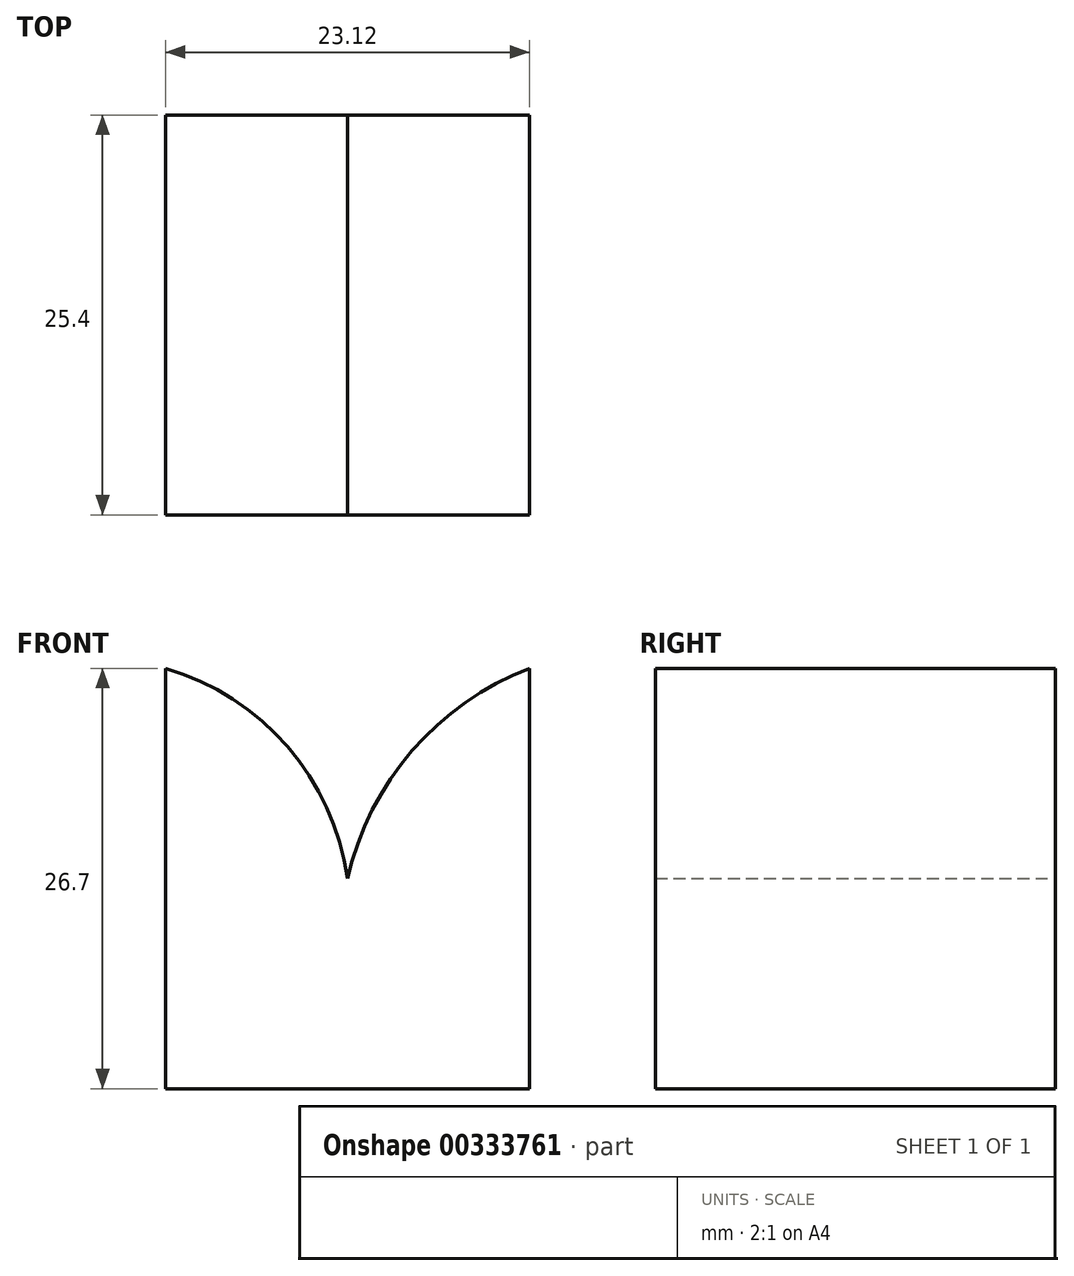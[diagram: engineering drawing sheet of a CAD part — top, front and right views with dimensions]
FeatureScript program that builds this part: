
annotation { "Feature Type Name" : "Feature", "Feature Type Description" : "" }
export const myFeature = defineFeature(function(context is Context, id is Id, definition is map)
    precondition{}
    {
        {
            var Q0;
            Q0=qCreatedBy(makeId("Front.planeOp"),FACE);
            var sketch = newSketch(context, id + "F0", { "sketchPlane" : qUnion([Q0])});
            skLineSegment(sketch, "E0.top", {"start": v(11.56, -13.35) * mm, "end": v(-11.56, -13.35) * mm});
            skLineSegment(sketch, "E0.left", {"start": v(11.56, 13.35) * mm, "end": v(11.56, -13.35) * mm});
            skLineSegment(sketch, "E0.right", {"start": v(-11.56, 13.35) * mm, "end": v(-11.56, -13.35) * mm});
            skPoint(sketch, "E0.middle", {"position": v(0, 0) * mm});
            skArc(sketch, "E1", {"start": v(11.56, 13.35) * mm, "mid": v(4.11, 8.12) * mm, "end": v(0, 0) * mm});
            skArc(sketch, "E2", {"start": v(0, 0) * mm, "mid": v(-3.81, 8.37) * mm, "end": v(-11.56, 13.35) * mm});
            skSolve(sketch);
        }
        {
            var Q0;
            Q0=makeQuery(id+"F0.imprint","IMPRINT",FACE,{"disambiguationData":[TD([[makeQuery(id+"F0.imprint","IMPRINT",EDGE,{"derivedFrom":sQuery(id+"F0.wireOp",EDGE,"E0.top")}),-1.0]])]});
            extrude(context, id + "F1", {"entities" : qUnion([Q0]), "depth" : 25.4 * mm});
        }
    });
